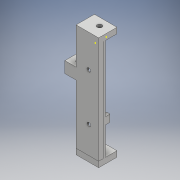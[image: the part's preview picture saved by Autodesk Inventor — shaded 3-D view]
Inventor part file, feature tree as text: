
AUTODESK INVENTOR PART (.ipt)
format: ipt  version: 2018 (Build 220112000, 112)  size: 344,064 bytes
history: native  units: mm
features: sketch x27, extrude x18, hole x6, fillet x3
ambient origin geometry x8: Origin, YZ Plane, XZ Plane, XY Plane, X Axis, Y Axis, Z Axis, Center Point
bodies: Solid1 (feature_tree)
feature tree (54):
  extrude  "Extrusion1"  Depth=100.0mm
  extrude  "Extrusion2"  Depth=5.0mm
  sketch  "Sketch3"  dims[d5=5.0mm d6=40.0mm d7=0.0mm]
  hole  "Hole1"  [1 undecoded]
  extrude  "Extrusion3"  Depth=23.0mm
  hole  "Hole2"  [1 undecoded]
  fillet  "Fillet1"  Radius=8.5mm
  extrude  "Extrusion4"  TaperAngle=90.0deg  [1 undecoded]
  extrude  "Extrusion5"  TaperAngle=180.0deg  [1 undecoded]
  hole  "Hole3"  [1 undecoded]
  fillet  "Fillet2"  Radius=3.5mm
  extrude  "Extrusion6"  Depth=10.0mm
  extrude  "Extrusion7"  Depth=5.0mm TaperAngle=0.0deg
  extrude  "Extrusion8"  Depth=5.0mm TaperAngle=0.0deg
  extrude  "Extrusion9"  Depth=0.1mm
  hole  "Hole4"  [1 undecoded]
  extrude  "Extrusion10"  Depth=5.5mm
  hole  "Hole5"  [1 undecoded]
  extrude  "Extrusion11"  Depth=2.1mm TaperAngle=0.0deg
  extrude  "Extrusion12"  Depth=5.0mm
  extrude  "Extrusion13"  Depth=1.0mm TaperAngle=0.0deg
  extrude  "Extrusion14"  Depth=3.8mm TaperAngle=0.0deg
  sketch  "Sketch21"  dims[d66=6.35mm d67=3.8mm d68=0.0mm]
  extrude  "Extrusion15"  Depth=4.55mm TaperAngle=0.0deg
  sketch  "Sketch23"  dims[d78=3.3mm d79=6.0mm d80=4.0mm d81=2.0mm d82=90.0deg d83=80.0mm d84=20.594885mm d85=5.45mm]
  extrude  "Extrusion16"  Depth=5.45mm
  extrude  "Extrusion17"  Depth=10.5mm
  hole  "Hole6"  [1 undecoded]
  fillet  "Fillet3"  Radius=4.5mm
  extrude  "Extrusion18"  Depth=15.5mm TaperAngle=0.0deg
  sketch  "Sketch1"  dims[d0=22.65mm d1=100.0mm]
  sketch  "Sketch2"  dims[d2=5.0mm d3=0.0mm d4=5.0mm]
  sketch  "Sketch4"  dims[d8=10.0mm]
  sketch  "Sketch5"  dims[d9=4.0mm d10=6.0mm d11=4.0mm d12=2.0mm d13=90.0deg d14=115.0mm d15=20.594885mm d16=23.0mm]
  sketch  "Sketch6"  dims[d17=102.75mm d18=0.0mm d19=1.175mm d20=8.5mm]
  sketch  "Sketch7"  dims[d21=21.0mm d22=90.0deg]
  sketch  "Sketch8"  dims[d23=8.5mm d24=180.0deg]
  sketch  "Sketch9"  dims[d25=21.0mm]
  sketch  "Sketch10"  dims[d26=4.0mm d27=6.0mm d28=4.0mm d29=2.0mm d30=90.0deg d31=115.0mm d32=20.594885mm d33=1.0mm d34=3.5mm]
  sketch  "Sketch11"  dims[d35=15.825mm d36=10.0mm]
  sketch  "Sketch12"  dims[d37=10.0mm d38=5.0mm d39=0.0mm]
  sketch  "Sketch13"  dims[d40=5.0mm d41=12.5mm d42=0.0mm]
  sketch  "Sketch14"  dims[d43=6.0mm d44=6.0mm d45=4.0mm d46=2.0mm d47=90.0deg d48=115.0mm d49=20.594885mm d50=0.1mm]
  sketch  "Sketch15"  dims[d51=4.25mm d52=1000.0mm d53=0.0mm]
  sketch  "Sketch16"  dims[d54=3.3mm d55=5.5mm]
  sketch  "Sketch17"  dims[d56=3.2mm d57=3.0mm]
  sketch  "Sketch18"  dims[d58=2.1mm d59=91.25mm d60=0.0mm]
  sketch  "Sketch19"  dims[d61=4.44mm d62=5.0mm]
  sketch  "Sketch20"  dims[d63=1.0mm d64=91.25mm d65=0.0mm]
  sketch  "Sketch22"  dims[d69=3.3mm d70=6.0mm d71=4.0mm d72=2.0mm d73=90.0deg d74=8.0mm d75=20.594885mm d76=4.55mm d77=0.0mm]
  sketch  "Sketch24"  dims[d86=129.8mm d87=0.0mm d88=10.5mm]
  sketch  "Sketch25"  dims[d89=2.5mm d90=0.0mm d91=10.0mm d92=4.5mm d93=0.0mm]
  sketch  "Sketch26"  dims[d94=8.0mm d95=0.0mm d96=15.5mm d97=0.0mm]
  sketch  "Sketch27"  dims[d98=10.0mm d99=10.0mm d100=4.1mm d101=0.0mm d102=5.0mm d103=17.5mm d104=10.0mm d105=0.0mm d106=5.0mm d107=6.0mm d108=6.0mm d109=4.0mm d110=2.0mm d111=90.0deg d112=80.0mm d113=20.594885mm d114=1.0mm d115=45.0mm d116=0.0mm]
note: 8 required parameter values undecoded (feature->parameter linkage not recoverable at this tier; creation-order binding heuristic only, values carry confidence <= 0.55)
